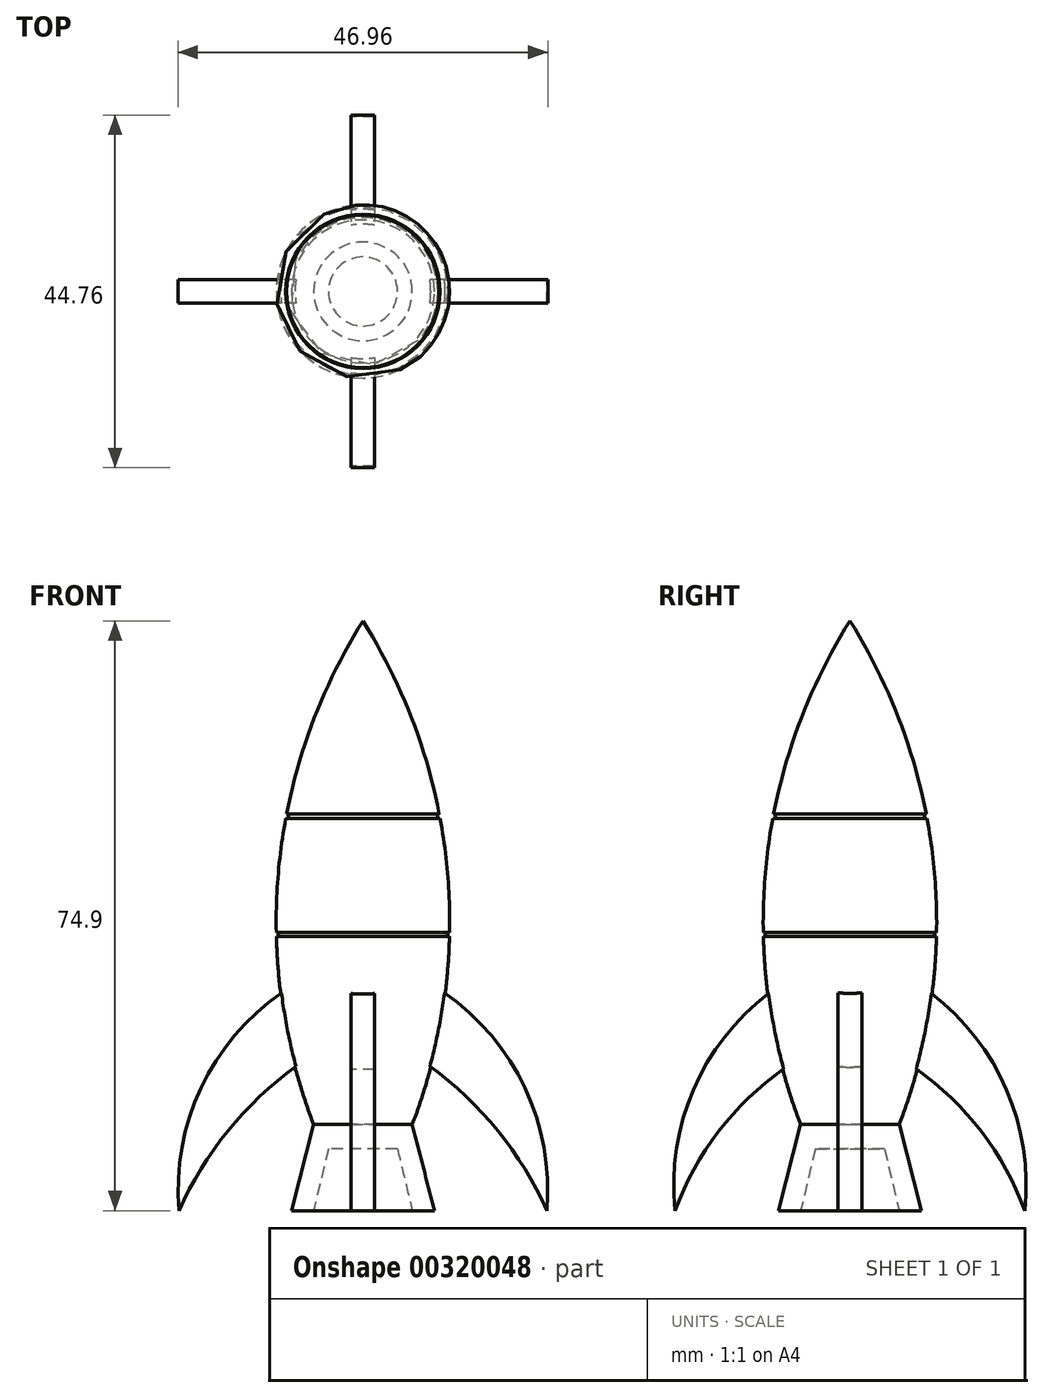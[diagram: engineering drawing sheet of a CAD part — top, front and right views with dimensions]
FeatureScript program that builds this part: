
annotation { "Feature Type Name" : "Feature", "Feature Type Description" : "" }
export const myFeature = defineFeature(function(context is Context, id is Id, definition is map)
    precondition{}
    {
        {
            var Q0;
            Q0=qCreatedBy(makeId("Front.planeOp"),FACE);
            var sketch = newSketch(context, id + "F0", { "sketchPlane" : qUnion([Q0])});
            skArc(sketch, "E0", {"start": v(0, 74.9) * mm, "mid": v(-5.98, 63.1) * mm, "end": v(-9.7, 50.4) * mm});
            skLineSegment(sketch, "E1", {"start": v(-6.26, 10.94) * mm, "end": v(-9.08, 0) * mm});
            skLineSegment(sketch, "E2", {"start": v(-9.08, 0) * mm, "end": v(-6.26, 0) * mm});
            skLineSegment(sketch, "E3", {"start": v(-6.26, 0) * mm, "end": v(-4.39, 7.86) * mm});
            skLineSegment(sketch, "E4", {"start": v(-4.39, 7.86) * mm, "end": v(0, 7.86) * mm});
            skLineSegment(sketch, "E5", {"start": v(0, 74.9) * mm, "end": v(0, 0) * mm});
            skPoint(sketch, "E6.end.orphan", {"position": v(0, 58.45) * mm});
            skPoint(sketch, "E7.end.orphan", {"position": v(0, 38.16) * mm});
            skArc(sketch, "E8", {"start": v(-11, 34.83) * mm, "mid": v(-10.75, 35.1) * mm, "end": v(-11, 35.34) * mm});
            skArc(sketch, "E9", {"start": v(-9.8, 49.8) * mm, "mid": v(-9.46, 50.05) * mm, "end": v(-9.7, 50.4) * mm});
            skArc(sketch, "E10.trimOffspring", {"start": v(-9.8, 49.8) * mm, "mid": v(-10.77, 42.6) * mm, "end": v(-11, 35.34) * mm});
            skArc(sketch, "E11.trimOffspring", {"start": v(-11, 34.83) * mm, "mid": v(-9.65, 22.69) * mm, "end": v(-6.26, 10.94) * mm});
            skSolve(sketch);
        }
        {
            var Q0;
            {var subQ0=sQuery(id+"F0.wireOp",EDGE,"E0");Q0=makeQuery(id+"F0.imprint","IMPRINT",FACE,{"disambiguationData":[TD([[makeQuery(id+"F0.imprint","IMPRINT",EDGE,{"derivedFrom":subQ0}),1.0]])]});}
            var Q1;
            Q1=sQuery(id+"F0.wireOp",EDGE,"E5");
            revolve(context, id + "F1", {"entities" : qUnion([Q0]), "axis" : qUnion([Q1]), "revolveType" : RevolveType.FULL});
        }
        {
            var Q0;
            Q0=qCreatedBy(makeId("Front.planeOp"),FACE);
            var sketch = newSketch(context, id + "F2", { "sketchPlane" : qUnion([Q0])});
            skArc(sketch, "E12", {"start": v(0, 32.3) * mm, "mid": v(-17.68, 20.49) * mm, "end": v(-23.37, 0) * mm});
            skArc(sketch, "E13", {"start": v(0, 23.15) * mm, "mid": v(-13.85, 13.77) * mm, "end": v(-23.37, 0) * mm});
            skLineSegment(sketch, "E14", {"start": v(0, 32.3) * mm, "end": v(0, 23.15) * mm});
            skArc(sketch, "E15.MirrorCS", {"start": v(0, 23.15) * mm, "mid": v(13.85, 13.77) * mm, "end": v(23.37, 0) * mm});
            skArc(sketch, "E16.MirrorCS", {"start": v(0, 32.3) * mm, "mid": v(17.68, 20.49) * mm, "end": v(23.37, 0) * mm});
            skSolve(sketch);
        }
        {
            var Q0;
            Q0 = qSketchRegion(id + "F2", true);
            extrude(context, id + "F3", {"entities" : qUnion([Q0]), "operationType" : NewBodyOperationType.ADD, "endBound" : BoundingType.SYMMETRIC, "depth" : 3 * mm});
        }
        {
            var Q0;
            Q0=qCreatedBy(makeId("Right.planeOp"),FACE);
            var sketch = newSketch(context, id + "F4", { "sketchPlane" : qUnion([Q0])});
            skArc(sketch, "E17", {"start": v(0, 32.7) * mm, "mid": v(-17.1, 20.43) * mm, "end": v(-22.2, 0) * mm});
            skArc(sketch, "E18", {"start": v(0, 22.47) * mm, "mid": v(-13.55, 13.65) * mm, "end": v(-22.2, 0) * mm});
            skLineSegment(sketch, "E19", {"start": v(0, 22.47) * mm, "end": v(0, 32.7) * mm});
            skArc(sketch, "E20.MirrorCS", {"start": v(0, 22.47) * mm, "mid": v(13.55, 13.65) * mm, "end": v(22.2, 0) * mm});
            skArc(sketch, "E21.MirrorCS", {"start": v(0, 32.7) * mm, "mid": v(17.1, 20.43) * mm, "end": v(22.2, 0) * mm});
            skSolve(sketch);
        }
        {
            var Q0;
            Q0 = qSketchRegion(id + "F4", true);
            extrude(context, id + "F5", {"entities" : qUnion([Q0]), "operationType" : NewBodyOperationType.ADD, "endBound" : BoundingType.SYMMETRIC, "depth" : 3 * mm});
        }
    });
